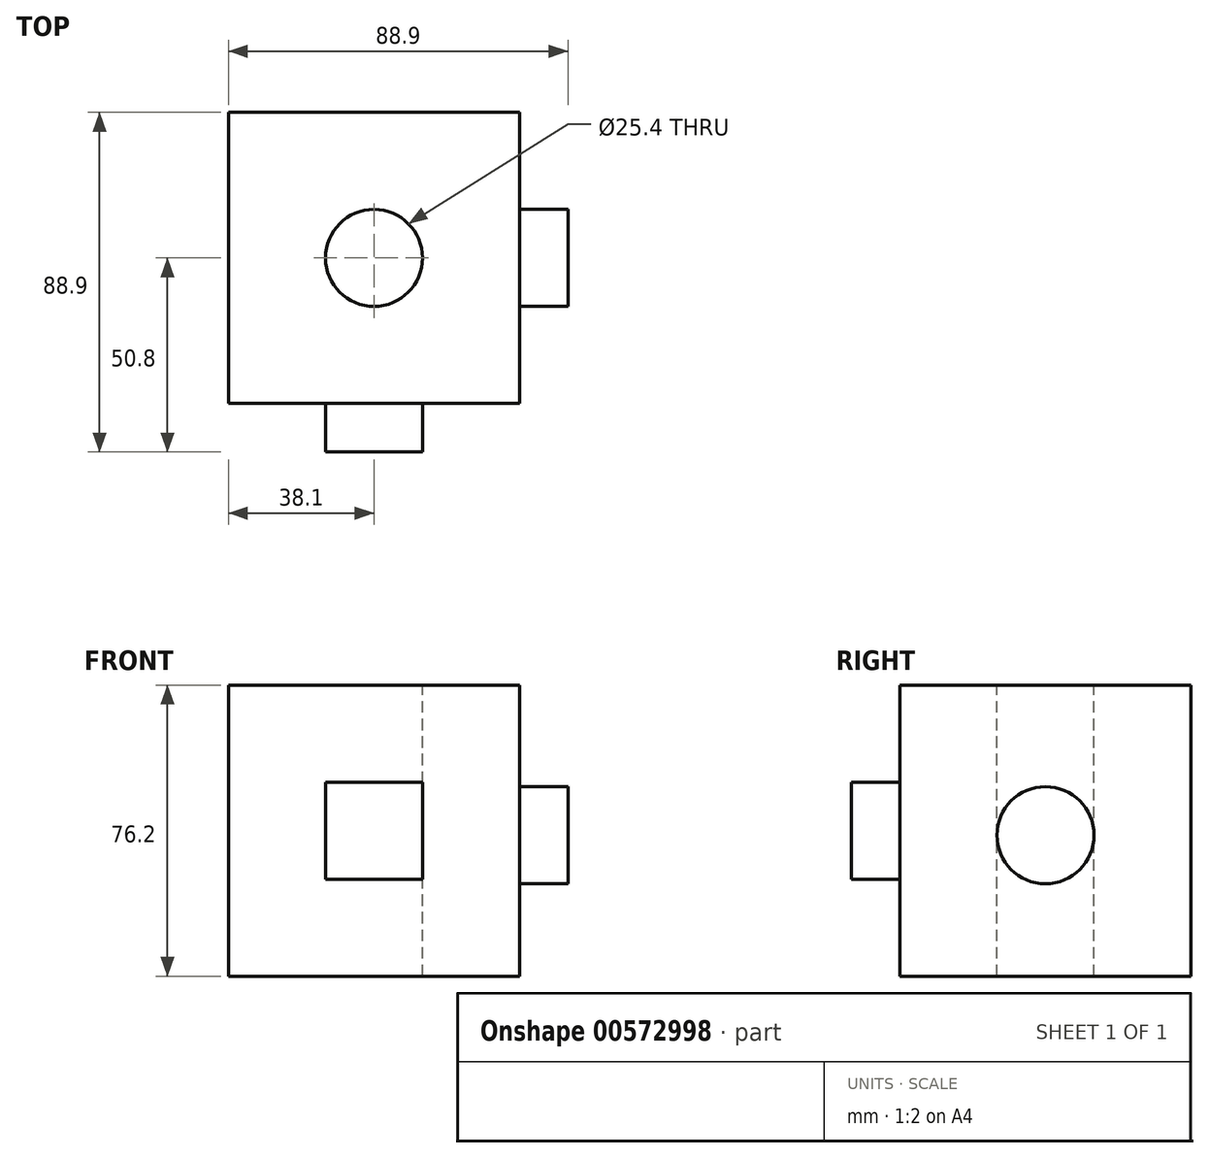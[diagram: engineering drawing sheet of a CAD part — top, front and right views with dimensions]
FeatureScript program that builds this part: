
annotation { "Feature Type Name" : "Feature", "Feature Type Description" : "" }
export const myFeature = defineFeature(function(context is Context, id is Id, definition is map)
    precondition{}
    {
        {
            var Q0;
            Q0=qCreatedBy(makeId("Front.planeOp"),FACE);
            var sketch = newSketch(context, id + "F0", { "sketchPlane" : qUnion([Q0])});
            skLineSegment(sketch, "E0.bottom", {"start": v(-70.79, 14.34) * mm, "end": v(5.41, 14.34) * mm});
            skLineSegment(sketch, "E0.top", {"start": v(-70.79, 90.54) * mm, "end": v(5.41, 90.54) * mm});
            skLineSegment(sketch, "E0.left", {"start": v(-70.79, 14.34) * mm, "end": v(-70.79, 90.54) * mm});
            skLineSegment(sketch, "E0.right", {"start": v(5.41, 14.34) * mm, "end": v(5.41, 90.54) * mm});
            skLineSegment(sketch, "E1.bottom", {"start": v(-32.69, 90.54) * mm, "end": v(-11.81, 90.54) * mm});
            skLineSegment(sketch, "E1.top", {"start": v(-32.69, 90.54) * mm, "end": v(-11.81, 90.54) * mm});
            skLineSegment(sketch, "E1.left", {"start": v(-32.69, 90.54) * mm, "end": v(-32.69, 90.54) * mm});
            skLineSegment(sketch, "E1.right", {"start": v(-11.81, 90.54) * mm, "end": v(-11.81, 90.54) * mm});
            skSolve(sketch);
        }
        {
            var Q0;
            Q0=makeQuery(id+"F0.imprint","IMPRINT",FACE,{"disambiguationData":[TD([[makeQuery(id+"F0.imprint","IMPRINT",EDGE,{"derivedFrom":sQuery(id+"F0.wireOp",EDGE,"E0.bottom")}),1.0]])]});
            extrude(context, id + "F1", {"entities" : qUnion([Q0]), "depth" : 76.2 * mm, "offsetDistance" : 25.4 * mm});
        }
        {
            var Q0;
            Q0=makeQuery(id+"F1.opExtrude","CAP_FACE",FACE,{"disambiguationData":[OSD([sQuery(id+"F0.wireOp",EDGE,"E0.bottom"),sQuery(id+"F0.wireOp",EDGE,"E0.top"),sQuery(id+"F0.wireOp",EDGE,"E0.left"),sQuery(id+"F0.wireOp",EDGE,"E0.right"),sQuery(id+"F0.wireOp",EDGE,"E1.top")])],"isStart":false});
            var sketch = newSketch(context, id + "F2", { "sketchPlane" : qUnion([Q0])});
            skLineSegment(sketch, "E2.bottom", {"start": v(-45.39, 65.14) * mm, "end": v(-19.99, 65.14) * mm});
            skLineSegment(sketch, "E2.top", {"start": v(-45.39, 39.74) * mm, "end": v(-19.99, 39.74) * mm});
            skLineSegment(sketch, "E2.left", {"start": v(-45.39, 65.14) * mm, "end": v(-45.39, 39.74) * mm});
            skLineSegment(sketch, "E2.right", {"start": v(-19.99, 65.14) * mm, "end": v(-19.99, 39.74) * mm});
            skSolve(sketch);
        }
        {
            var Q0;
            Q0=makeQuery(id+"F2.imprint","IMPRINT",FACE,{"disambiguationData":[TD([[makeQuery(id+"F2.imprint","IMPRINT",EDGE,{"derivedFrom":sQuery(id+"F2.wireOp",EDGE,"E2.bottom")}),-1.0]])]});
            extrude(context, id + "F3", {"entities" : qUnion([Q0]), "operationType" : NewBodyOperationType.ADD, "depth" : 12.7 * mm, "offsetDistance" : 25.4 * mm});
        }
        {
            var Q0;
            Q0=makeQuery(id+"F1.opExtrude","SWEPT_FACE",FACE,{"disambiguationData":[OSD([sQuery(id+"F0.wireOp",EDGE,"E0.right")])]});
            var sketch = newSketch(context, id + "F4", { "sketchPlane" : qUnion([Q0])});
            skCircle(sketch, "E3", {"center": v(-38.1, 51.24) * mm, "radius": 12.7 * mm});
            skSolve(sketch);
        }
        {
            var Q0;
            Q0=makeQuery(id+"F4.imprint","IMPRINT",FACE,{"disambiguationData":[TD([[makeQuery(id+"F4.imprint","IMPRINT",EDGE,{"derivedFrom":sQuery(id+"F4.wireOp",EDGE,"E3")}),1.0]])]});
            extrude(context, id + "F5", {"entities" : qUnion([Q0]), "operationType" : NewBodyOperationType.ADD, "depth" : 12.7 * mm, "offsetDistance" : 25.4 * mm});
        }
        {
            var Q0;
            Q0=makeQuery(id+"F1.opExtrude","SWEPT_FACE",FACE,{"disambiguationData":[OSD([sQuery(id+"F0.wireOp",EDGE,"E0.top"),sQuery(id+"F0.wireOp",EDGE,"E1.top")])]});
            var sketch = newSketch(context, id + "F6", { "sketchPlane" : qUnion([Q0])});
            skPoint(sketch, "E4", {"position": v(-32.69, -38.1) * mm});
            skSolve(sketch);
        }
        {
            var Q0;
            Q0=sQuery(id+"F6.wireOp",VERTEX,"E4");
            var Q1;
            Q1=makeQuery(id+"F1.opExtrude","SWEPT_BODY",BODY,{"disambiguationData":[OSD([sQuery(id+"F0.wireOp",EDGE,"E0.bottom"),sQuery(id+"F0.wireOp",EDGE,"E0.top"),sQuery(id+"F0.wireOp",EDGE,"E0.left"),sQuery(id+"F0.wireOp",EDGE,"E0.right"),sQuery(id+"F0.wireOp",EDGE,"E1.top")])]});
            hole(context, id + "F7", {"style" : HoleStyle.SIMPLE, "endStyle" : HoleEndStyle.THROUGH, "holeDiameter" : 25.4 * mm, "isTappedThrough" : true, "tappedDepth" : 12.7 * mm, "tapClearance" : 3, "locations" : qUnion([Q0]), "scope" : qUnion([Q1])});
        }
    });
